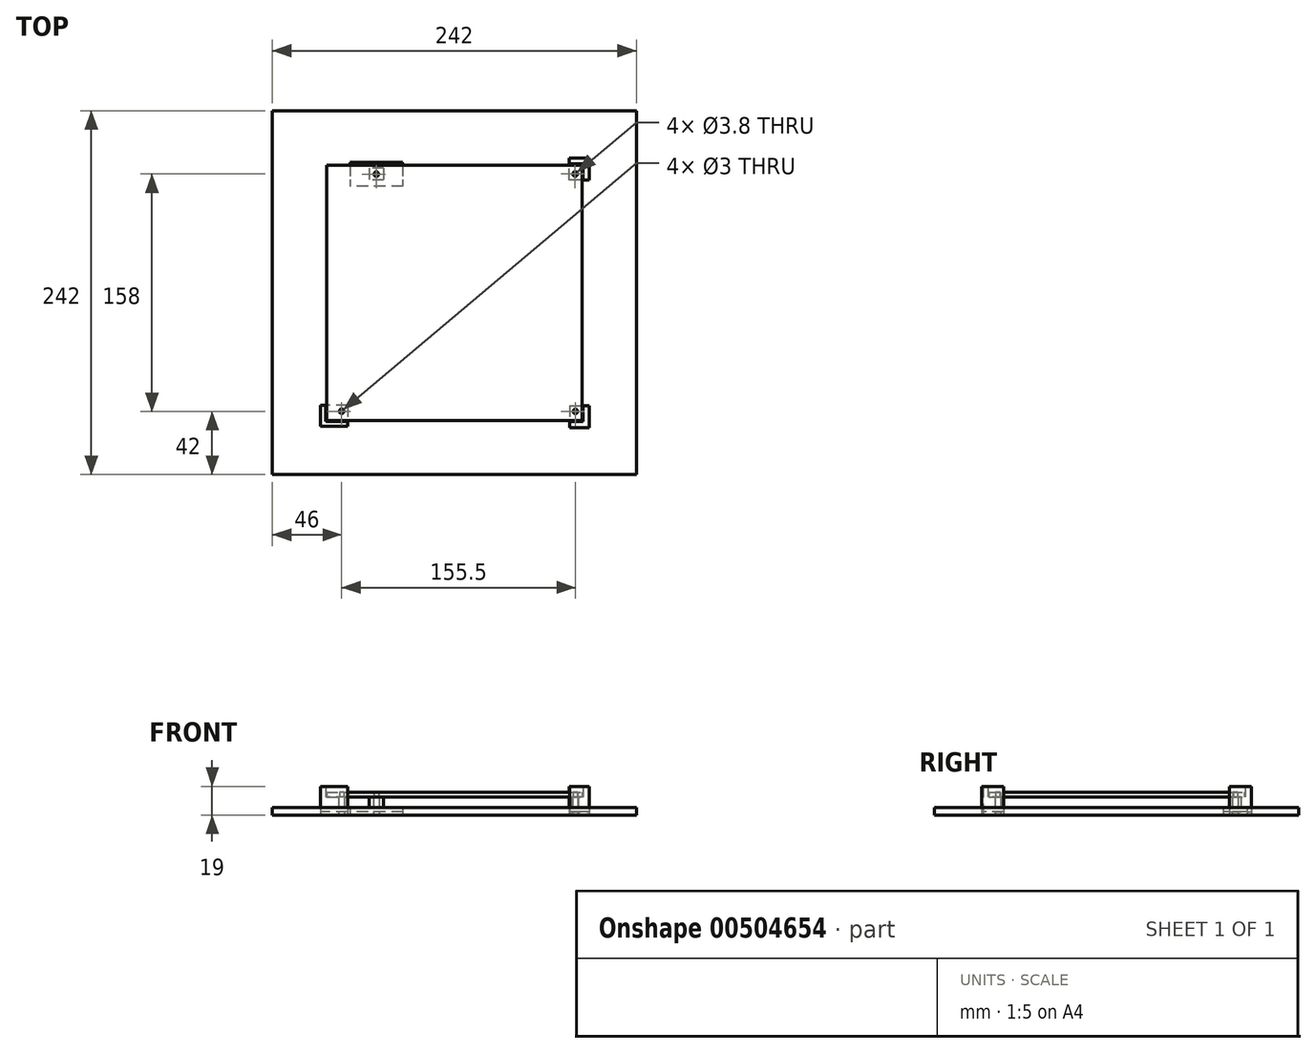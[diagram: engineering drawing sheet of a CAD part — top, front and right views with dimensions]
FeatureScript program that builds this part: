
annotation { "Feature Type Name" : "Feature", "Feature Type Description" : "" }
export const myFeature = defineFeature(function(context is Context, id is Id, definition is map)
    precondition{}
    {
        {
            var Q0;
            Q0=qCreatedBy(makeId("Top.planeOp"),FACE);
            var sketch = newSketch(context, id + "F0", { "sketchPlane" : qUnion([Q0])});
            skLineSegment(sketch, "E0.bottom", {"start": v(10, 10) * mm, "end": v(180, 10) * mm});
            skLineSegment(sketch, "E0.top", {"start": v(10, 180) * mm, "end": v(180, 180) * mm});
            skLineSegment(sketch, "E0.left", {"start": v(10, 10) * mm, "end": v(10, 180) * mm});
            skLineSegment(sketch, "E0.right", {"start": v(180, 10) * mm, "end": v(180, 180) * mm});
            skSolve(sketch);
        }
        {
            var Q0;
            Q0=qCreatedBy(makeId("Top.planeOp"),FACE);
            var sketch = newSketch(context, id + "F1", { "sketchPlane" : qUnion([Q0])});
            skCircle(sketch, "E1", {"center": v(175.5, 16) * mm, "radius": 1.5 * mm});
            skPoint(sketch, "E2", {"position": v(174, 16) * mm});
            skPoint(sketch, "E3", {"position": v(177, 16) * mm});
            skPoint(sketch, "E4", {"position": v(175.5, 14.5) * mm});
            skCircle(sketch, "E5", {"center": v(20, 16.1) * mm, "radius": 1.5 * mm});
            skPoint(sketch, "E6", {"position": v(18.5, 16.1) * mm});
            skPoint(sketch, "E7", {"position": v(20, 14.6) * mm});
            skCircle(sketch, "E8", {"center": v(43.1, 173.9) * mm, "radius": 1.5 * mm});
            skPoint(sketch, "E9", {"position": v(41.6, 173.9) * mm});
            skPoint(sketch, "E10", {"position": v(43.1, 175.4) * mm});
            skCircle(sketch, "E11", {"center": v(175.3, 174) * mm, "radius": 1.5 * mm});
            skPoint(sketch, "E12", {"position": v(175.3, 175.5) * mm});
            skPoint(sketch, "E13", {"position": v(176.8, 174) * mm});
            skSolve(sketch);
        }
        {
            var Q0;
            Q0=qCreatedBy(makeId("Top.planeOp"),FACE);
            var sketch = newSketch(context, id + "F2", { "sketchPlane" : qUnion([Q0])});
            skCircle(sketch, "E14.0", {"center": v(20, 16.1) * mm, "radius": 1.9 * mm});
            skCircle(sketch, "E15.0", {"center": v(175.5, 16) * mm, "radius": 1.9 * mm});
            skCircle(sketch, "E16.0", {"center": v(175.3, 174) * mm, "radius": 1.9 * mm});
            skCircle(sketch, "E17.0", {"center": v(43.1, 173.9) * mm, "radius": 1.9 * mm});
            skLineSegment(sketch, "E18.bottom", {"start": v(23.9, 20) * mm, "end": v(16.1, 20) * mm});
            skLineSegment(sketch, "E18.top", {"start": v(23.9, 12.2) * mm, "end": v(16.1, 12.2) * mm, "construction": true});
            skLineSegment(sketch, "E18.left", {"start": v(23.9, 20) * mm, "end": v(23.9, 12.2) * mm});
            skLineSegment(sketch, "E18.right", {"start": v(16.1, 20) * mm, "end": v(16.1, 12.2) * mm});
            skLineSegment(sketch, "E19.bottom", {"start": v(23.9, 20) * mm, "end": v(6, 20) * mm});
            skLineSegment(sketch, "E19.top", {"start": v(23.9, 6.2) * mm, "end": v(6, 6.2) * mm});
            skLineSegment(sketch, "E19.left", {"start": v(23.9, 20) * mm, "end": v(23.9, 6.2) * mm});
            skLineSegment(sketch, "E19.right", {"start": v(6, 20) * mm, "end": v(6, 6.2) * mm});
            skLineSegment(sketch, "E20.bottom", {"start": v(179.4, 19.9) * mm, "end": v(171.6, 19.9) * mm});
            skLineSegment(sketch, "E20.top", {"start": v(179.4, 12.1) * mm, "end": v(171.6, 12.1) * mm, "construction": true});
            skLineSegment(sketch, "E20.left", {"start": v(179.4, 19.9) * mm, "end": v(179.4, 12.1) * mm});
            skLineSegment(sketch, "E20.right", {"start": v(171.6, 19.9) * mm, "end": v(171.6, 12.1) * mm});
            skLineSegment(sketch, "E21.bottom", {"start": v(171.6, 19.9) * mm, "end": v(184.7, 19.9) * mm});
            skLineSegment(sketch, "E21.top", {"start": v(171.6, 5.3) * mm, "end": v(184.7, 5.3) * mm});
            skLineSegment(sketch, "E21.left", {"start": v(171.6, 19.9) * mm, "end": v(171.6, 5.3) * mm});
            skLineSegment(sketch, "E21.right", {"start": v(184.7, 19.9) * mm, "end": v(184.7, 5.3) * mm});
            skLineSegment(sketch, "E22.bottom", {"start": v(179.2, 177.9) * mm, "end": v(171.4, 177.9) * mm});
            skLineSegment(sketch, "E22.top", {"start": v(179.2, 170.1) * mm, "end": v(171.4, 170.1) * mm});
            skLineSegment(sketch, "E22.left", {"start": v(179.2, 177.9) * mm, "end": v(179.2, 170.1) * mm, "construction": true});
            skLineSegment(sketch, "E22.right", {"start": v(171.4, 177.9) * mm, "end": v(171.4, 170.1) * mm});
            skLineSegment(sketch, "E23.bottom", {"start": v(48, 177.8) * mm, "end": v(38.2, 177.8) * mm});
            skLineSegment(sketch, "E23.top", {"start": v(48, 170) * mm, "end": v(38.2, 170) * mm});
            skLineSegment(sketch, "E23.left", {"start": v(48, 177.8) * mm, "end": v(48, 170) * mm});
            skLineSegment(sketch, "E23.right", {"start": v(38.2, 177.8) * mm, "end": v(38.2, 170) * mm});
            skLineSegment(sketch, "E24.bottom", {"start": v(60.6, 181.8) * mm, "end": v(25.6, 181.8) * mm});
            skLineSegment(sketch, "E24.top", {"start": v(60.6, 166) * mm, "end": v(25.6, 166) * mm});
            skLineSegment(sketch, "E24.left", {"start": v(60.6, 181.8) * mm, "end": v(60.6, 166) * mm});
            skLineSegment(sketch, "E24.right", {"start": v(25.6, 181.8) * mm, "end": v(25.6, 166) * mm});
            skLineSegment(sketch, "E25.bottom", {"start": v(23.9, 20) * mm, "end": v(9.3, 20) * mm});
            skLineSegment(sketch, "E25.top", {"start": v(23.9, 9.3) * mm, "end": v(9.3, 9.3) * mm});
            skLineSegment(sketch, "E25.left", {"start": v(23.9, 20) * mm, "end": v(23.9, 9.3) * mm});
            skLineSegment(sketch, "E25.right", {"start": v(9.3, 20) * mm, "end": v(9.3, 9.3) * mm});
            skLineSegment(sketch, "E26.bottom", {"start": v(171.6, 19.9) * mm, "end": v(180.7, 19.9) * mm});
            skLineSegment(sketch, "E26.top", {"start": v(171.6, 9.3) * mm, "end": v(180.7, 9.3) * mm});
            skLineSegment(sketch, "E26.left", {"start": v(171.6, 19.9) * mm, "end": v(171.6, 9.3) * mm});
            skLineSegment(sketch, "E26.right", {"start": v(180.7, 19.9) * mm, "end": v(180.7, 9.3) * mm});
            skLineSegment(sketch, "E27.bottom", {"start": v(171.4, 170.1) * mm, "end": v(180.7, 170.1) * mm});
            skLineSegment(sketch, "E27.top", {"start": v(171.4, 180.7) * mm, "end": v(180.7, 180.7) * mm});
            skLineSegment(sketch, "E27.left", {"start": v(171.4, 170.1) * mm, "end": v(171.4, 180.7) * mm});
            skLineSegment(sketch, "E27.right", {"start": v(180.7, 170.1) * mm, "end": v(180.7, 180.7) * mm});
            skLineSegment(sketch, "E28.bottom", {"start": v(171.4, 170.1) * mm, "end": v(184.7, 170.1) * mm});
            skLineSegment(sketch, "E28.top", {"start": v(171.4, 184.7) * mm, "end": v(184.7, 184.7) * mm});
            skLineSegment(sketch, "E28.left", {"start": v(171.4, 170.1) * mm, "end": v(171.4, 184.7) * mm});
            skLineSegment(sketch, "E28.right", {"start": v(184.7, 170.1) * mm, "end": v(184.7, 184.7) * mm});
            skSolve(sketch);
        }
        {
            var Q0;
            Q0=qCreatedBy(makeId("Front.planeOp"),FACE);
            var sketch = newSketch(context, id + "F3", { "sketchPlane" : qUnion([Q0])});
            skLineSegment(sketch, "E29", {"start": v(-119.23, 0) * mm, "end": v(-119.23, 12) * mm, "construction": true});
            skLineSegment(sketch, "E30", {"start": v(-119.23, 12) * mm, "end": v(-119.23, 19) * mm, "construction": true});
            skLineSegment(sketch, "E31", {"start": v(-171.62, 12) * mm, "end": v(-171.62, 15) * mm, "construction": true});
            skSolve(sketch);
        }
        {
            var Q0;
            Q0=makeQuery(id+"F0.imprint","IMPRINT",FACE,{"disambiguationData":[TD([[makeQuery(id+"F0.imprint","IMPRINT",EDGE,{"derivedFrom":sQuery(id+"F0.wireOp",EDGE,"E0.bottom")}),1.0]])]});
            var Q1;
            Q1=sQuery(id+"F3.wireOp",VERTEX,"E31.end");
            var Q2;
            Q2=sQuery(id+"F3.wireOp",VERTEX,"E31.start");
            extrude(context, id + "F4", {"entities" : qUnion([Q0]), "endBound" : BoundingType.UP_TO_VERTEX, "endBoundEntityVertex" : qUnion([Q1]), "depth" : 25 * mm, "hasSecondDirection" : true, "secondDirectionBound" : SecondDirectionBoundingType.UP_TO_VERTEX, "secondDirectionOppositeDirection" : false, "secondDirectionBoundEntityVertex" : qUnion([Q2]), "secondDirectionDepth" : 25 * mm});
        }
        {
            var Q0;
            Q0=makeQuery(id+"F1.imprint","IMPRINT",FACE,{"disambiguationData":[TD([[makeQuery(id+"F1.imprint","IMPRINT",EDGE,{"derivedFrom":sQuery(id+"F1.wireOp",EDGE,"E8")}),1.0]])]});
            var Q1;
            Q1=makeQuery(id+"F1.imprint","IMPRINT",FACE,{"disambiguationData":[TD([[makeQuery(id+"F1.imprint","IMPRINT",EDGE,{"derivedFrom":sQuery(id+"F1.wireOp",EDGE,"E11")}),1.0]])]});
            var Q2;
            Q2=makeQuery(id+"F1.imprint","IMPRINT",FACE,{"disambiguationData":[TD([[makeQuery(id+"F1.imprint","IMPRINT",EDGE,{"derivedFrom":sQuery(id+"F1.wireOp",EDGE,"E5")}),1.0]])]});
            var Q3;
            Q3=makeQuery(id+"F1.imprint","IMPRINT",FACE,{"disambiguationData":[TD([[makeQuery(id+"F1.imprint","IMPRINT",EDGE,{"derivedFrom":sQuery(id+"F1.wireOp",EDGE,"E1")}),1.0]])]});
            var Q4;
            Q4=sQuery(id+"F1.wireOp",EDGE,"E5");
            var Q5;
            Q5=sQuery(id+"F1.wireOp",EDGE,"E1");
            var Q6;
            Q6=sQuery(id+"F1.wireOp",EDGE,"E11");
            var Q7;
            Q7=sQuery(id+"F1.wireOp",EDGE,"E8");
            extrude(context, id + "F5", {"entities" : qUnion([Q0, Q1, Q2, Q3]), "operationType" : NewBodyOperationType.REMOVE, "surfaceEntities" : qUnion([Q4, Q5, Q6, Q7]), "depth" : 25 * mm});
        }
        {
            var Q0;
            Q0=makeQuery(id+"F2.imprint","IMPRINT",FACE,{"disambiguationData":[TD([[makeQuery(id+"F2.imprint","IMPRINT",EDGE,{"derivedFrom":sQuery(id+"F2.wireOp",EDGE,"E14.0")}),-1.0]])]});
            var Q1;
            Q1=makeQuery(id+"F2.imprint","IMPRINT",FACE,{"disambiguationData":[TD([[makeQuery(id+"F2.imprint","IMPRINT",EDGE,{"derivedFrom":sQuery(id+"F2.wireOp",EDGE,"E15.0")}),-1.0]])]});
            var Q2;
            Q2=makeQuery(id+"F2.imprint","IMPRINT",FACE,{"disambiguationData":[TD([[makeQuery(id+"F2.imprint","IMPRINT",EDGE,{"derivedFrom":sQuery(id+"F2.wireOp",EDGE,"E16.0")}),-1.0]])]});
            var Q3;
            Q3=makeQuery(id+"F2.imprint","IMPRINT",FACE,{"disambiguationData":[TD([[makeQuery(id+"F2.imprint","IMPRINT",EDGE,{"derivedFrom":sQuery(id+"F2.wireOp",EDGE,"E17.0")}),-1.0]])]});
            var Q4;
            Q4=sQuery(id+"F3.wireOp",VERTEX,"E30.start");
            extrude(context, id + "F6", {"entities" : qUnion([Q0, Q1, Q2, Q3]), "endBound" : BoundingType.UP_TO_VERTEX, "endBoundEntityVertex" : qUnion([Q4]), "depth" : 25 * mm});
        }
        {
            var Q0;
            Q0=makeQuery(id+"F2.imprint","IMPRINT",FACE,{"disambiguationData":[TD([[makeQuery(id+"F2.imprint","IMPRINT",EDGE,{"derivedFrom":sQuery(id+"F2.wireOp",EDGE,"E19.bottom")}),1.0]])]});
            var Q1;
            Q1=makeQuery(id+"F2.imprint","IMPRINT",FACE,{"disambiguationData":[TD([[makeQuery(id+"F2.imprint","IMPRINT",EDGE,{"derivedFrom":sQuery(id+"F2.wireOp",EDGE,"E21.bottom")}),-1.0]])]});
            var Q2;
            {var subQ4=sQuery(id+"F2.wireOp",EDGE,"E27.top");Q2=makeQuery(id+"F2.imprint","IMPRINT",FACE,{"disambiguationData":[TD([[makeQuery(id+"F2.imprint","IMPRINT",EDGE,{"derivedFrom":subQ4}),1.0]])]});}
            var Q3;
            Q3=sQuery(id+"F3.wireOp",VERTEX,"E30.end");
            extrude(context, id + "F7", {"entities" : qUnion([Q0, Q1, Q2]), "operationType" : NewBodyOperationType.ADD, "endBound" : BoundingType.UP_TO_VERTEX, "endBoundEntityVertex" : qUnion([Q3]), "depth" : 12 * mm});
        }
        {
            var Q0;
            Q0=makeQuery(id+"F2.imprint","IMPRINT",FACE,{"disambiguationData":[TD([[makeQuery(id+"F2.imprint","IMPRINT",EDGE,{"derivedFrom":sQuery(id+"F2.wireOp",EDGE,"E23.bottom")}),-1.0]])]});
            extrude(context, id + "F8", {"entities" : qUnion([Q0]), "operationType" : NewBodyOperationType.ADD, "depth" : 5 * mm});
        }
        {
            var Q0;
            Q0=qCreatedBy(makeId("Top.planeOp"),FACE);
            var sketch = newSketch(context, id + "F9", { "sketchPlane" : qUnion([Q0])});
            skLineSegment(sketch, "E32.0", {"start": v(-26, -26) * mm, "end": v(216, -26) * mm});
            skLineSegment(sketch, "E32.1", {"start": v(-26, -26) * mm, "end": v(-26, 216) * mm});
            skLineSegment(sketch, "E32.2", {"start": v(-26, 216) * mm, "end": v(216, 216) * mm});
            skLineSegment(sketch, "E32.3", {"start": v(216, -26) * mm, "end": v(216, 216) * mm});
            skSolve(sketch);
        }
        {
            var Q0;
            Q0=makeQuery(id+"F9.imprint","IMPRINT",FACE,{"disambiguationData":[TD([[makeQuery(id+"F9.imprint","IMPRINT",EDGE,{"derivedFrom":sQuery(id+"F9.wireOp",EDGE,"E32.0")}),1.0]])]});
            extrude(context, id + "F10", {"entities" : qUnion([Q0]), "depth" : 5 * mm});
        }
        {
            var Q0;
            {var subQ0=sQuery(id+"F2.wireOp",EDGE,"E25.right");var subQ1=sQuery(id+"F2.wireOp",EDGE,"E25.top");Q0=makeQuery(id+"F7.boolean.opBoolean","MERGE",FACE,{"derivedFrom":[makeQuery(id+"F6.opExtrude","CAP_FACE",FACE,{"disambiguationData":[OSD([sQuery(id+"F2.wireOp",EDGE,"E14.0"),sQuery(id+"F2.wireOp",EDGE,"E25.bottom"),subQ1,sQuery(id+"F2.wireOp",EDGE,"E25.left"),subQ0])],"isStart":true}),makeQuery(id+"F7.opExtrude","CAP_FACE",FACE,{"disambiguationData":[OSD([sQuery(id+"F2.wireOp",EDGE,"E19.bottom"),sQuery(id+"F2.wireOp",EDGE,"E19.top"),sQuery(id+"F2.wireOp",EDGE,"E19.left"),sQuery(id+"F2.wireOp",EDGE,"E19.right"),subQ1,subQ0])],"isStart":true})]});}
            var Q1;
            {var subQ0=sQuery(id+"F2.wireOp",EDGE,"E26.right");var subQ1=sQuery(id+"F2.wireOp",EDGE,"E26.top");Q1=makeQuery(id+"F7.boolean.opBoolean","MERGE",FACE,{"derivedFrom":[makeQuery(id+"F6.opExtrude","CAP_FACE",FACE,{"disambiguationData":[OSD([sQuery(id+"F2.wireOp",EDGE,"E15.0"),sQuery(id+"F2.wireOp",EDGE,"E26.bottom"),subQ1,sQuery(id+"F2.wireOp",EDGE,"E26.left"),subQ0])],"isStart":true}),makeQuery(id+"F7.opExtrude","CAP_FACE",FACE,{"disambiguationData":[OSD([sQuery(id+"F2.wireOp",EDGE,"E21.bottom"),sQuery(id+"F2.wireOp",EDGE,"E21.top"),sQuery(id+"F2.wireOp",EDGE,"E21.left"),sQuery(id+"F2.wireOp",EDGE,"E21.right"),subQ1,subQ0])],"isStart":true})]});}
            var Q2;
            {var subQ0=sQuery(id+"F2.wireOp",EDGE,"E23.right");var subQ1=sQuery(id+"F2.wireOp",EDGE,"E23.left");var subQ2=sQuery(id+"F2.wireOp",EDGE,"E23.top");var subQ3=sQuery(id+"F2.wireOp",EDGE,"E23.bottom");Q2=makeQuery(id+"F8.boolean.opBoolean","MERGE",FACE,{"derivedFrom":[makeQuery(id+"F6.opExtrude","CAP_FACE",FACE,{"disambiguationData":[OSD([sQuery(id+"F2.wireOp",EDGE,"E17.0"),subQ3,subQ2,subQ1,subQ0])],"isStart":true}),makeQuery(id+"F8.opExtrude","CAP_FACE",FACE,{"disambiguationData":[OSD([subQ3,subQ2,subQ1,subQ0,sQuery(id+"F2.wireOp",EDGE,"E24.bottom"),sQuery(id+"F2.wireOp",EDGE,"E24.top"),sQuery(id+"F2.wireOp",EDGE,"E24.left"),sQuery(id+"F2.wireOp",EDGE,"E24.right")])],"isStart":true})]});}
            var Q3;
            {var subQ0=sQuery(id+"F2.wireOp",EDGE,"E28.left");var subQ1=sQuery(id+"F2.wireOp",EDGE,"E28.bottom");var subQ2=sQuery(id+"F2.wireOp",EDGE,"E27.right");var subQ3=sQuery(id+"F2.wireOp",EDGE,"E27.top");Q3=makeQuery(id+"F7.boolean.opBoolean","MERGE",FACE,{"derivedFrom":[makeQuery(id+"F6.opExtrude","CAP_FACE",FACE,{"disambiguationData":[OSD([sQuery(id+"F2.wireOp",EDGE,"E16.0"),subQ3,subQ2,subQ1,subQ0])],"isStart":true}),makeQuery(id+"F7.opExtrude","CAP_FACE",FACE,{"disambiguationData":[OSD([subQ3,subQ2,subQ1,sQuery(id+"F2.wireOp",EDGE,"E28.top"),subQ0,sQuery(id+"F2.wireOp",EDGE,"E28.right")])],"isStart":true})]});}
            extrude(context, id + "F11", {"entities" : qUnion([Q0, Q1, Q2, Q3]), "operationType" : NewBodyOperationType.REMOVE, "oppositeDirection" : true, "depth" : 2 * mm});
        }
    });
